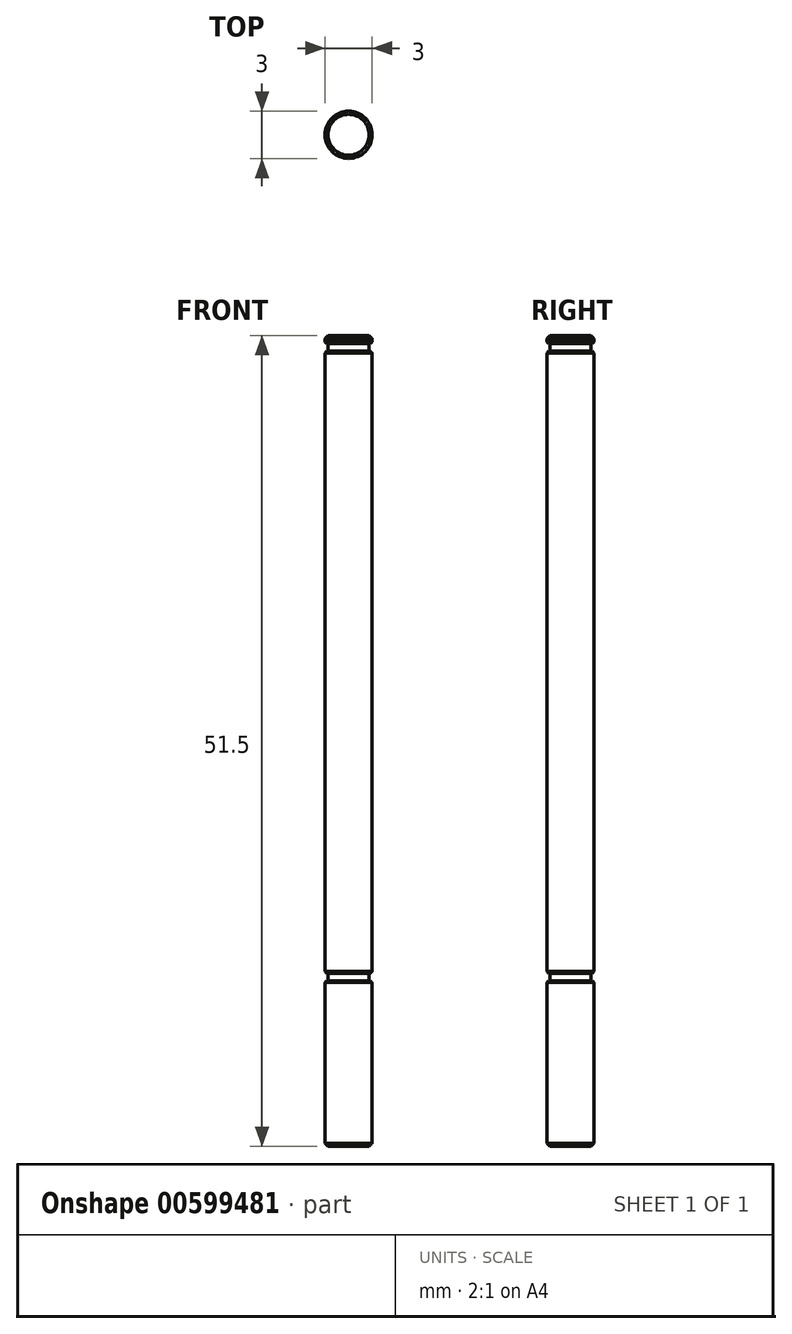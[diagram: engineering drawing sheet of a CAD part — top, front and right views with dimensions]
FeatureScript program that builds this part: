
annotation { "Feature Type Name" : "Feature", "Feature Type Description" : "" }
export const myFeature = defineFeature(function(context is Context, id is Id, definition is map)
    precondition{}
    {
        {
            var Q0;
            Q0=qCreatedBy(makeId("Top.planeOp"),FACE);
            var sketch = newSketch(context, id + "F0", { "sketchPlane" : qUnion([Q0])});
            skCircle(sketch, "E0", {"center": v(0, 0) * mm, "radius": 1.5 * mm});
            skCircle(sketch, "E1.0", {"center": v(0, 0) * mm, "radius": 1.3 * mm});
            skSolve(sketch);
        }
        {
            var Q0;
            Q0=qSketchRegion(id+"F0",true);
            var Q1;
            Q1=makeQuery(id+"F0.imprint","IMPRINT",FACE,{"disambiguationData":[TD([[makeQuery(id+"F0.imprint","IMPRINT",EDGE,{"derivedFrom":sQuery(id+"F0.wireOp",EDGE,"E1.0")}),1.0]])]});
            extrude(context, id + "F1", {"entities" : qUnion([Q0, Q1]), "depth" : 39.5 * mm, "offsetDistance" : 25 * mm});
        }
        {
            var Q0;
            Q0=makeQuery(id+"F0.imprint","IMPRINT",FACE,{"disambiguationData":[TD([[makeQuery(id+"F0.imprint","IMPRINT",EDGE,{"derivedFrom":sQuery(id+"F0.wireOp",EDGE,"E1.0")}),1.0]])]});
            extrude(context, id + "F2", {"entities" : qUnion([Q0]), "operationType" : NewBodyOperationType.ADD, "oppositeDirection" : true, "depth" : 1 * mm});
        }
        {
            var Q0;
            Q0=qSketchRegion(id+"F0",true);
            extrude(context, id + "F3", {"entities" : qUnion([Q0]), "operationType" : NewBodyOperationType.ADD, "oppositeDirection" : true, "depth" : 1 * mm, "hasSecondDirection" : true, "secondDirectionOppositeDirection" : true, "secondDirectionDepth" : 0.5 * mm});
        }
        {
            var Q0;
            {var subQ0=sQuery(id+"F0.wireOp",EDGE,"E1.0");Q0=makeQuery(id+"F3.boolean.opBoolean","MERGE",FACE,{"derivedFrom":[makeQuery(id+"F2.opExtrude","CAP_FACE",FACE,{"disambiguationData":[OSD([subQ0])],"isStart":false}),makeQuery(id+"F3.opExtrude","CAP_FACE",FACE,{"disambiguationData":[OSD([sQuery(id+"F0.wireOp",EDGE,"E0"),subQ0])],"isStart":false})]});}
            extrude(context, id + "F4", {"entities" : qUnion([Q0]), "operationType" : NewBodyOperationType.ADD, "depth" : 10 * mm});
        }
        {
            var Q0;
            Q0=makeQuery(id+"F1.opExtrude","CAP_FACE",FACE,{"disambiguationData":[OSD([sQuery(id+"F0.wireOp",EDGE,"E0")])],"isStart":false});
            var sketch = newSketch(context, id + "F5", { "sketchPlane" : qUnion([Q0])});
            skCircle(sketch, "E2.0", {"center": v(0, 0) * mm, "radius": 1.3 * mm});
            skSolve(sketch);
        }
        {
            var Q0;
            Q0=makeQuery(id+"F5.imprint","IMPRINT",FACE,{"disambiguationData":[TD([[makeQuery(id+"F5.imprint","IMPRINT",EDGE,{"derivedFrom":sQuery(id+"F5.wireOp",EDGE,"E2.0")}),1.0]])]});
            extrude(context, id + "F6", {"entities" : qUnion([Q0]), "operationType" : NewBodyOperationType.ADD, "depth" : 1 * mm, "offsetDistance" : 25 * mm});
        }
        {
            var Q0;
            Q0=makeQuery(id+"F1.opExtrude","CAP_FACE",FACE,{"disambiguationData":[OSD([sQuery(id+"F0.wireOp",EDGE,"E0")])],"isStart":false});
            extrude(context, id + "F7", {"entities" : qUnion([Q0]), "operationType" : NewBodyOperationType.ADD, "depth" : 1 * mm, "offsetDistance" : 25 * mm, "hasSecondDirection" : true, "secondDirectionOppositeDirection" : false, "secondDirectionDepth" : 0.5 * mm});
        }
        {
            var Q0;
            Q0=makeQuery(id+"F7.opExtrude","CAP_EDGE",EDGE,{"disambiguationData":[OSD([sQuery(id+"F0.wireOp",EDGE,"E0")])],"isStart":false});
            var Q1;
            Q1=makeQuery(id+"F4.opExtrude","CAP_EDGE",EDGE,{"disambiguationData":[OSD([sQuery(id+"F0.wireOp",EDGE,"E0")])],"isStart":false});
            chamfer(context, id + "F8", {"entities" : qUnion([Q0, Q1]), "width" : 0.2 * mm, "tangentPropagation" : true});
        }
        {
            var Q0;
            Q0=makeQuery(id+"F1.opExtrude","CAP_EDGE",EDGE,{"disambiguationData":[OSD([sQuery(id+"F0.wireOp",EDGE,"E0")])],"isStart":false});
            var Q1;
            Q1=makeQuery(id+"F7.opExtrude","CAP_EDGE",EDGE,{"disambiguationData":[OSD([sQuery(id+"F0.wireOp",EDGE,"E0")])],"isStart":true});
            var Q2;
            Q2=makeQuery(id+"F1.opExtrude","CAP_EDGE",EDGE,{"disambiguationData":[OSD([sQuery(id+"F0.wireOp",EDGE,"E0")])],"isStart":true});
            var Q3;
            Q3=makeQuery(id+"F3.opExtrude","CAP_EDGE",EDGE,{"disambiguationData":[OSD([sQuery(id+"F0.wireOp",EDGE,"E0")])],"isStart":true});
            chamfer(context, id + "F9", {"entities" : qUnion([Q0, Q1, Q2, Q3]), "width" : 0.1 * mm, "tangentPropagation" : true});
        }
    });
